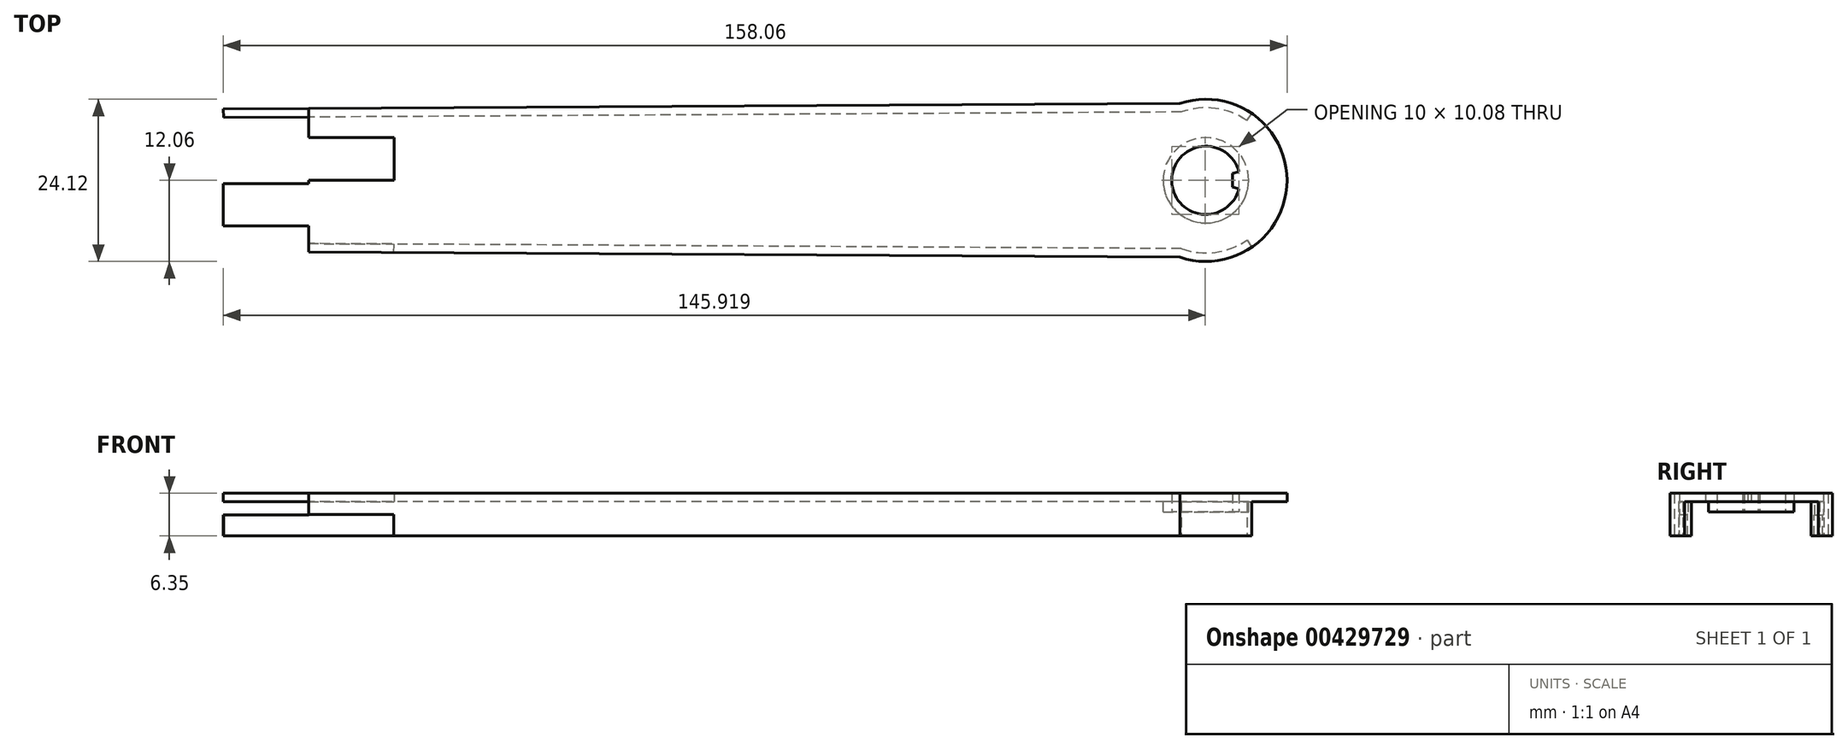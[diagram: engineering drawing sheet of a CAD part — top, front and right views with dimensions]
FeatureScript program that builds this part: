
annotation { "Feature Type Name" : "Feature", "Feature Type Description" : "" }
export const myFeature = defineFeature(function(context is Context, id is Id, definition is map)
    precondition{}
    {
        {
            var Q0;
            Q0=qCreatedBy(makeId("Top.planeOp"),FACE);
            var sketch = newSketch(context, id + "F0", { "sketchPlane" : qUnion([Q0])});
            skPoint(sketch, "E0", {"position": v(-133.35, 0) * mm});
            skPoint(sketch, "E1", {"position": v(133.35, 0) * mm});
            skCircle(sketch, "E2", {"center": v(-133.35, 0) * mm, "radius": 10.16 * mm});
            skCircle(sketch, "E3", {"center": v(133.35, 0) * mm, "radius": 12.06 * mm});
            skPoint(sketch, "E4", {"position": v(-131.1, 9.9) * mm});
            skPoint(sketch, "E5", {"position": v(-131.1, -9.9) * mm});
            skPoint(sketch, "E6", {"position": v(129.49, 11.43) * mm});
            skPoint(sketch, "E7", {"position": v(129.49, -11.43) * mm});
            skPoint(sketch, "E8", {"position": v(-133.35, 10.16) * mm});
            skPoint(sketch, "E9", {"position": v(133.35, 12.06) * mm});
            skLineSegment(sketch, "E10", {"start": v(129.49, -11.43) * mm, "end": v(-131.1, -9.9) * mm});
            skLineSegment(sketch, "E11", {"start": v(129.49, 11.43) * mm, "end": v(-131.1, 9.9) * mm});
            skPoint(sketch, "E12", {"position": v(0, 20.26) * mm});
            skPoint(sketch, "E13", {"position": v(0, -19.52) * mm});
            skLineSegment(sketch, "E14", {"start": v(0, -19.52) * mm, "end": v(0, 20.26) * mm});
            skSolve(sketch);
        }
        {
            var Q0;
            {var subQ0=sQuery(id+"F0.wireOp",EDGE,"E10");var subQ1=sQuery(id+"F0.wireOp",EDGE,"E3");var subQ2=makeQuery(id+"F0.imprint","INTERSECT",VERTEX,{"derivedFrom":[subQ1,subQ0]});Q0=makeQuery(id+"F0.imprint","IMPRINT",FACE,{"disambiguationData":[TD([[makeQuery(id+"F0.imprint","IMPRINT",EDGE,{"disambiguationData":[TD([[subQ2,1.0]])],"derivedFrom":subQ1}),-1.0]])]});}
            var Q1;
            {var subQ0=sQuery(id+"F0.wireOp",EDGE,"E3");var subQ1=makeQuery(id+"F0.imprint","INTERSECT",VERTEX,{"derivedFrom":[subQ0,sQuery(id+"F0.wireOp",EDGE,"E10")]});Q1=makeQuery(id+"F0.imprint","IMPRINT",FACE,{"disambiguationData":[TD([[makeQuery(id+"F0.imprint","IMPRINT",EDGE,{"disambiguationData":[TD([[subQ1,1.0]])],"derivedFrom":subQ0}),1.0]])]});}
            extrude(context, id + "F1", {"entities" : qUnion([Q0, Q1]), "depth" : 6.35 * mm});
        }
        {
            var Q0;
            Q0=makeQuery(id+"F1.opExtrude","CAP_FACE",FACE,{"disambiguationData":[OSD([sQuery(id+"F0.wireOp",EDGE,"E3"),sQuery(id+"F0.wireOp",EDGE,"E10"),sQuery(id+"F0.wireOp",EDGE,"E11"),sQuery(id+"F0.wireOp",EDGE,"E14")])],"isStart":true});
            var Q1;
            Q1=makeQuery(id+"F1.opExtrude","SWEPT_FACE",FACE,{"disambiguationData":[OSD([sQuery(id+"F0.wireOp",EDGE,"E14")])]});
            shell(context, id + "F2", {"entities" : qUnion([Q0, Q1]), "thickness" : 1.27 * mm});
        }
        {
            var Q0;
            Q0=makeQuery(id+"F2.opShell","OFFSET_FACE",FACE,{"disambiguationData":[OSD([sQuery(id+"F0.wireOp",EDGE,"E3"),sQuery(id+"F0.wireOp",EDGE,"E10"),sQuery(id+"F0.wireOp",EDGE,"E11"),sQuery(id+"F0.wireOp",EDGE,"mjLNaLwQ-FFsS-bJik-TmkY-nE4KQvV5gACF"),sQuery(id+"F0.wireOp",EDGE,"31WK7Zx6-OMev-ZD63-Uo4U-srRC2rB3krrJ")])]});
            var sketch = newSketch(context, id + "F3", { "sketchPlane" : qUnion([Q0])});
            skPoint(sketch, "E15", {"position": v(0, 0) * mm});
            skLineSegment(sketch, "E16.bottom", {"start": v(0, 0) * mm, "end": v(12.75, 0) * mm});
            skLineSegment(sketch, "E16.top", {"start": v(0, -6.35) * mm, "end": v(12.75, -6.35) * mm});
            skLineSegment(sketch, "E16.left", {"start": v(0, 0) * mm, "end": v(0, -6.35) * mm});
            skLineSegment(sketch, "E16.right", {"start": v(12.75, 0) * mm, "end": v(12.75, -6.35) * mm});
            skSolve(sketch);
        }
        {
            var Q0;
            {var subQ0=sQuery(id+"F3.wireOp",EDGE,"E16.right");Q0=makeQuery(id+"F3.imprint","IMPRINT",FACE,{"disambiguationData":[TD([[makeQuery(id+"F3.imprint","IMPRINT",EDGE,{"derivedFrom":subQ0}),-1.0]])]});}
            extrude(context, id + "F4", {"entities" : qUnion([Q0]), "operationType" : NewBodyOperationType.REMOVE, "oppositeDirection" : true, "depth" : 25.4 * mm});
        }
        {
            var Q0;
            Q0=makeQuery(id+"F2.opShell","OFFSET_FACE",FACE,{"disambiguationData":[OSD([sQuery(id+"F0.wireOp",EDGE,"E3"),sQuery(id+"F0.wireOp",EDGE,"E10"),sQuery(id+"F0.wireOp",EDGE,"E11"),sQuery(id+"F0.wireOp",EDGE,"E14")])]});
            var sketch = newSketch(context, id + "F5", { "sketchPlane" : qUnion([Q0])});
            skPoint(sketch, "E17", {"position": v(0, 0.5) * mm});
            skLineSegment(sketch, "E18.bottom", {"start": v(0, 0.5) * mm, "end": v(-12.65, 0.5) * mm});
            skLineSegment(sketch, "E18.top", {"start": v(0, 6.8) * mm, "end": v(-12.65, 6.8) * mm});
            skLineSegment(sketch, "E18.left", {"start": v(0, 0.5) * mm, "end": v(0, 6.8) * mm});
            skLineSegment(sketch, "E18.right", {"start": v(-12.65, 0.5) * mm, "end": v(-12.65, 6.8) * mm});
            skSolve(sketch);
        }
        {
            var Q0;
            Q0=makeQuery(id+"F5.imprint","IMPRINT",FACE,{"disambiguationData":[TD([[makeQuery(id+"F5.imprint","IMPRINT",EDGE,{"derivedFrom":sQuery(id+"F5.wireOp",EDGE,"E18.bottom")}),-1.0]])]});
            extrude(context, id + "F6", {"entities" : qUnion([Q0]), "operationType" : NewBodyOperationType.ADD, "oppositeDirection" : true, "depth" : 1.27 * mm});
        }
        {
            var Q0;
            Q0=makeQuery(id+"F1.opExtrude","SWEPT_FACE",FACE,{"disambiguationData":[OSD([sQuery(id+"F0.wireOp",EDGE,"E11")])]});
            var sketch = newSketch(context, id + "F7", { "sketchPlane" : qUnion([Q0])});
            skLineSegment(sketch, "E19.bottom", {"start": v(-0.06, 0) * mm, "end": v(12.59, 0) * mm});
            skLineSegment(sketch, "E19.top", {"start": v(-0.06, 3.12) * mm, "end": v(12.59, 3.12) * mm});
            skLineSegment(sketch, "E19.left", {"start": v(-0.06, 0) * mm, "end": v(-0.06, 3.12) * mm});
            skLineSegment(sketch, "E19.right", {"start": v(12.59, 0) * mm, "end": v(12.59, 3.12) * mm});
            skSolve(sketch);
        }
        {
            var Q0;
            Q0=makeQuery(id+"F7.imprint","IMPRINT",FACE,{"disambiguationData":[TD([[makeQuery(id+"F7.imprint","IMPRINT",EDGE,{"derivedFrom":sQuery(id+"F7.wireOp",EDGE,"E19.bottom")}),1.0]])]});
            extrude(context, id + "F8", {"entities" : qUnion([Q0]), "operationType" : NewBodyOperationType.ADD, "oppositeDirection" : true, "depth" : 1.27 * mm});
        }
        {
            var Q0;
            Q0=makeQuery(id+"F2.opShell","OFFSET_FACE",FACE,{"disambiguationData":[OSD([sQuery(id+"F0.wireOp",EDGE,"E10")])]});
            var sketch = newSketch(context, id + "F9", { "sketchPlane" : qUnion([Q0])});
            skLineSegment(sketch, "E20.bottom", {"start": v(0, 0) * mm, "end": v(-12.75, 0) * mm});
            skLineSegment(sketch, "E20.top", {"start": v(0, 3.18) * mm, "end": v(-12.75, 3.17) * mm});
            skLineSegment(sketch, "E20.left", {"start": v(0, 0) * mm, "end": v(0, 3.18) * mm});
            skLineSegment(sketch, "E20.right", {"start": v(-12.75, 0) * mm, "end": v(-12.75, 3.17) * mm});
            skSolve(sketch);
        }
        {
            var Q0;
            {var subQ4=sQuery(id+"F9.wireOp",EDGE,"E20.right");Q0=makeQuery(id+"F9.imprint","IMPRINT",FACE,{"disambiguationData":[TD([[makeQuery(id+"F9.imprint","IMPRINT",EDGE,{"derivedFrom":subQ4}),-1.0]])]});}
            extrude(context, id + "F10", {"entities" : qUnion([Q0]), "operationType" : NewBodyOperationType.REMOVE, "oppositeDirection" : true, "depth" : 25.4 * mm});
        }
        {
            var Q0;
            Q0=makeQuery(id+"F6.boolean.opBoolean","MERGE",FACE,{"derivedFrom":[makeQuery(id+"F2.opShell","OFFSET_FACE",FACE,{"disambiguationData":[OSD([sQuery(id+"F0.wireOp",EDGE,"E3"),sQuery(id+"F0.wireOp",EDGE,"E10"),sQuery(id+"F0.wireOp",EDGE,"E11"),sQuery(id+"F0.wireOp",EDGE,"E14")])]}),makeQuery(id+"F6.opExtrude","CAP_FACE",FACE,{"disambiguationData":[OSD([sQuery(id+"F5.wireOp",EDGE,"E18.bottom"),sQuery(id+"F5.wireOp",EDGE,"E18.top"),sQuery(id+"F5.wireOp",EDGE,"E18.left"),sQuery(id+"F5.wireOp",EDGE,"E18.right")])],"isStart":true})]});
            var sketch = newSketch(context, id + "F11", { "sketchPlane" : qUnion([Q0])});
            skPoint(sketch, "E21", {"position": v(133.35, 0) * mm});
            skCircle(sketch, "E22", {"center": v(133.35, 0) * mm, "radius": 6.35 * mm});
            skSolve(sketch);
        }
        {
            var Q0;
            Q0=makeQuery(id+"F11.imprint","IMPRINT",FACE,{"disambiguationData":[TD([[makeQuery(id+"F11.imprint","IMPRINT",EDGE,{"derivedFrom":sQuery(id+"F11.wireOp",EDGE,"E22")}),1.0]])]});
            extrude(context, id + "F12", {"entities" : qUnion([Q0]), "operationType" : NewBodyOperationType.ADD, "depth" : 1.52 * mm});
        }
        {
            var Q0;
            Q0=makeQuery(id+"F12.opExtrude","CAP_FACE",FACE,{"disambiguationData":[OSD([sQuery(id+"F11.wireOp",EDGE,"E22")])],"isStart":false});
            var sketch = newSketch(context, id + "F13", { "sketchPlane" : qUnion([Q0])});
            skCircle(sketch, "E23", {"center": v(133.35, 0) * mm, "radius": 5.08 * mm});
            skPoint(sketch, "E24", {"position": v(138.27, 1.27) * mm});
            skPoint(sketch, "E25", {"position": v(138.27, -1.27) * mm});
            skPoint(sketch, "E26", {"position": v(137.31, 1.02) * mm});
            skPoint(sketch, "E27", {"position": v(137.31, -1.02) * mm});
            skLineSegment(sketch, "E28", {"start": v(138.27, 1.27) * mm, "end": v(137.31, 1.02) * mm});
            skLineSegment(sketch, "E29", {"start": v(137.31, 1.02) * mm, "end": v(137.31, -1.02) * mm});
            skLineSegment(sketch, "E30", {"start": v(137.31, -1.02) * mm, "end": v(138.27, -1.27) * mm});
            skSolve(sketch);
        }
        {
            var Q0;
            {var subQ0=sQuery(id+"F13.wireOp",EDGE,"E28");Q0=makeQuery(id+"F13.imprint","IMPRINT",FACE,{"disambiguationData":[TD([[makeQuery(id+"F13.imprint","IMPRINT",EDGE,{"derivedFrom":subQ0}),-1.0]])]});}
            extrude(context, id + "F14", {"entities" : qUnion([Q0]), "operationType" : NewBodyOperationType.REMOVE, "oppositeDirection" : true, "depth" : 25.4 * mm});
        }
        {
            var Q0;
            Q0=makeQuery(id+"F8.boolean.opBoolean","MERGE",FACE,{"derivedFrom":[makeQuery(id+"F1.opExtrude","CAP_FACE",FACE,{"disambiguationData":[OSD([sQuery(id+"F0.wireOp",EDGE,"E3"),sQuery(id+"F0.wireOp",EDGE,"E10"),sQuery(id+"F0.wireOp",EDGE,"E11"),sQuery(id+"F0.wireOp",EDGE,"E14")])],"isStart":true}),makeQuery(id+"F8.opExtrude","SWEPT_FACE",FACE,{"disambiguationData":[OSD([sQuery(id+"F7.wireOp",EDGE,"E19.bottom")])]})]});
            var sketch = newSketch(context, id + "F15", { "sketchPlane" : qUnion([Q0])});
            skPoint(sketch, "E31", {"position": v(139.47, 8.9) * mm});
            skPoint(sketch, "E32", {"position": v(139.47, -8.89) * mm});
            skPoint(sketch, "E33", {"position": v(140.2, 9.94) * mm});
            skPoint(sketch, "E34", {"position": v(140.2, -9.94) * mm});
            skPoint(sketch, "E35", {"position": v(133.35, 0) * mm});
            skLineSegment(sketch, "E36", {"start": v(133.35, 0) * mm, "end": v(140.2, 9.94) * mm});
            skLineSegment(sketch, "E37", {"start": v(133.35, 0) * mm, "end": v(140.2, -9.94) * mm});
            skSolve(sketch);
        }
        {
            var Q0;
            {var subQ0=sQuery(id+"F15.wireOp",EDGE,"E36");var subQ1=sQuery(id+"F0.wireOp",EDGE,"E3");var subQ2=makeQuery(id+"F1.opExtrude","CAP_EDGE",EDGE,{"disambiguationData":[OSD([subQ1])],"isStart":true});var subQ3=makeQuery(id+"F15.imprint","INTERSECT",VERTEX,{"derivedFrom":[subQ2,subQ0]});Q0=makeQuery(id+"F15.imprint","IMPRINT",FACE,{"disambiguationData":[TD([[makeQuery(id+"F15.imprint","IMPRINT",EDGE,{"disambiguationData":[TD([[subQ3,-1.0]])],"derivedFrom":subQ2}),-1.0]])]});}
            var Q1;
            Q1=makeQuery(id+"F6.boolean.opBoolean","MERGE",FACE,{"derivedFrom":[makeQuery(id+"F2.opShell","OFFSET_FACE",FACE,{"disambiguationData":[OSD([sQuery(id+"F0.wireOp",EDGE,"E3"),sQuery(id+"F0.wireOp",EDGE,"E10"),sQuery(id+"F0.wireOp",EDGE,"E11"),sQuery(id+"F0.wireOp",EDGE,"E14")])]}),makeQuery(id+"F6.opExtrude","CAP_FACE",FACE,{"disambiguationData":[OSD([sQuery(id+"F5.wireOp",EDGE,"E18.bottom"),sQuery(id+"F5.wireOp",EDGE,"E18.top"),sQuery(id+"F5.wireOp",EDGE,"E18.left"),sQuery(id+"F5.wireOp",EDGE,"E18.right")])],"isStart":true})]});
            extrude(context, id + "F16", {"entities" : qUnion([Q0]), "operationType" : NewBodyOperationType.REMOVE, "endBound" : BoundingType.UP_TO_SURFACE, "oppositeDirection" : true, "endBoundEntityFace" : qUnion([Q1]), "depth" : 25.4 * mm});
        }
    });
